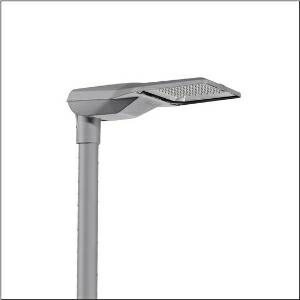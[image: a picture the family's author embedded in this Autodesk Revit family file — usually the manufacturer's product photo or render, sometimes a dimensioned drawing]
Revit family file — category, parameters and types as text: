
# Revit family: streetlight_sl_21_iq_midi___p0_8ab_5xe3r31g08mb_fd1f
name_source: partatom
category: Lighting Fixtures
units: mm (PartAtom-declared; Revit-internal decimal feet)

## family parameters
Cut with Voids When Loaded = No
Host = Face
Light Source = No
Part Type = Normal
Room Calculation Point = No
Round Connector Dimension = Use Diameter
Shared = No

## types (1)
- --- (1 x LED, 16930 lm, 146.7 W, 3000K)
    Apparent Load = 147 VA
    CIE Flux Codes = 36 71 98 100 100
    Color Rendering = 70
    Color Temperature = 3000K
    Default Elevation = 1800 mm
    Description = Streetlight SL 21 iQ midi, mast luminaire, primary light control with lens, of PMMA, primary optical cover: cover, of toughened safety glass, transparent, light distribution: P0.8aB, light emission: direct distribution, primary light characteristic: asymmetric, installation type: post-top, side-entry, LED, High Power LED, rated luminous flux: 16.930lm, luminous efficacy: 115lm/W, light colour: 730, colour temperature: 3000K, control gear: iQ Street-Remote, control: pre-setting: linear dimming characteristic, Street-Remote, Auto-Match, Temp-Guard, Lumen-Switch, Night-Set, Smart-Wire, Light-Fading, Desk-Remote (wireless, voltage-free reading and setting of iQ features in the workshop via application-optimized NFC function/RFID function), optimised constant luminous flux control (CLO 2.0), mains connection: 230..240V, AC, 50/60Hz, start of lifetime: 147W, end of service life: 161W, reduction: 62W, luminaire housing, of diecast aluminium, powder-coated, Siteco® metallic grey (DB 702S), corrosivity category C5 mid according to DIN EN ISO 12944, please order mast flange separately, inclination adjustable: 0°, 5°, 10°, 15°, sealing non-destructively replaceable, multi-level sealing system, length: 644mm, width: 335mm, height: 110mm, mast flange for spigot size: 42mm (side-entry): 5XC10008XM4, 60/48mm (side-entry/post-top): 5XC10108XM2, 76/60mm (side-entry/post-top): 5XC10108XM1, mounting height: 4..8m, protection rating (complete): IP66, insulation class (complete): insulation class II (safety insulation), certification: CE, ENEC, ENEC+, VDE, impact resistance: IK10, permissible operating ambient temperature for outdoor applications: -40..+50°C, standard-compliant lighting for roads and squares, packaging unit: 1 piece

Light Distribution: P0.8aB
    Height = 111 mm
    Lamp = 1 x LED
    Lamp Light Flux = 16930 lm
    Lamp Power = 146.7 W
    Lamp count = 1
    Length = 644 mm
    Luminous efficacy = 115 lm/W
    Manufacturer = Siteco
    ModVariant = No
    Model = 5XE3R31G08MB
    Number of Poles = 1
    OnlyDefault = Yes
    Power Factor = 1
    Product Name = Streetlight SL 21 iQ midi | P0.8aB
    Product group = mast luminaire | pylon top
    ProductGroupID = 6100
    Protection Class = Protection class II
    Protection Degree = IP 66
    RLX_Detail_Level = 1
    RLX_Emergency_Light_Flux = 0 lm
    RLX_Emergency_Type = 0
    RLX_Emergency_Type_DB = No
    RlxData = <blob elided: 26549 chars, md5=2fc76309>
    Socket = socket
    Standby Power = 0 W
    System Light Flux = 16931 lm
    System Power = 147 W
    Type Comments = factory setting: luminous flux: 100 % | dim-lin: 254 | 753 mA
    Type Image = l_1004298.jpg
    URL = http://relux.com
    VarID = @adj_074370
    Voltage = 0 V
    Weight = 0.00 kg
    Width = 336 mm

## geometry (parser evidence)
native form markers: Blend x4, Sweep x11
no freeform markers — native parametric forms only
